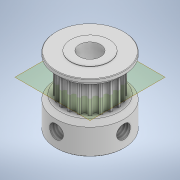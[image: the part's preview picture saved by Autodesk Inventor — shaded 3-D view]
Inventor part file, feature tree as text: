
AUTODESK INVENTOR PART (.ipt)
format: ipt  version: 2020 (Build 240168000, 168)  size: 311,808 bytes
history: native  units: mm
features: plane x4, sketch x4, extrude x2, mirror x2, chamfer x2, projected_geometry x2, revolve x1, hole x1, pattern_circular x1
ambient origin geometry x8: Origin, YZ Plane, XZ Plane, XY Plane, X Axis, Y Axis, Z Axis, Center Point
bodies: Solid1 (feature_tree)
feature tree (19):
  revolve  "Revolution1"  [1 undecoded]
  extrude  "Extrusion1"  Depth=7.0mm
  plane  "Work Plane1"
  mirror  "Mirror1"
  chamfer  "Chamfer2"  Angle=90.0deg  [1 undecoded]
  chamfer  "Chamfer1"  Distance=0.1mm
  plane  "Work Plane2"
  hole  "Hole1"  [1 undecoded]
  plane  "Work Plane3"
  mirror  "Mirror2"
  extrude  "Extrusion2"  Depth=0.555mm
  pattern_circular  "Circular Pattern1"  [2 undecoded]
  plane  "Work Plane4"
  sketch  "Sketch1"  dims[d0=8.0mm d1=2.5mm]
  sketch  "Sketch2"  dims[d2=16.0mm d3=7.0mm]
  projected_geometry  "Projected Loop1"
  sketch  "Sketch3"  dims[d4=7.1mm]
  sketch  "Sketch5"  dims[d5=6.11mm d6=90.0deg d8=0.1mm d9=0.0mm d10=0.125mm d11=2.0mm d12=45.0deg d13=3.242mm d14=8.0mm d15=5.5mm d16=2.0mm d17=90.0deg d18=11.8mm d19=20.594885mm d22=12.22mm d23=0.15mm d24=0.555mm d25=0.75mm d26=0.1mm d27=0.0mm d28=200.0mm d29=360.0deg d31=1.0mm d32=2.0mm d33=45.0deg d34=9.0mm]
  projected_geometry  "Project Cut Edges2"
note: 5 required parameter values undecoded (feature->parameter linkage not recoverable at this tier; creation-order binding heuristic only, values carry confidence <= 0.55)